# Revit family: PRD_AR_TpsAndWtrSpplOtltFttngs_FittingUnit_AQFU0230-AQFU0234 2
name_source: partatom
category: Plumbing Fixtures
units: mm (PartAtom-declared; Revit-internal decimal feet)

## family parameters
Always vertical = Yes
Cut with Voids When Loaded = No
Enable Cutting in Views = No
Maintain Annotation Orientation = No
OmniClass Number = 23.45.55.11
OmniClass Title = Sanitary Components
Part Type = Normal
Room Calculation Point = No
Round Connector Dimension = Use Diameter
Shared = No
Work Plane-Based = No

## types (5) — shared parameters
AssetType = Fixed
BodyMaterial = PRD_AR_StainlessSteel_SatinFinished
Category = Pr_40_20_87, Taps and water supply outlet fittings
Circulation = no
Export Type to IFC As = IfcDistributionChamberElementType
Finish = satin finished
Fitting = separately
FlowColdWater = 0.0 L/s
FlowHotWater = 0.0 L/s
HygieneFlushing = no
IfcExportAs = IfcDistributionChamberElement
IfcExportType = USERDEFINED
InletConversionSize = 25  [stored 0.082021 ft]
InletSize = G1B
Manufacturer = KWC Group Management AG
ManufacturerName = KWC Group Management AG
ManufacturerURL = www.kwc-professional.com
Material = stainless steel
NominalDepth = 73 mm  [stored 0.239501 ft]
NominalHeight = 470 mm  [stored 1.54199 ft]
OutletSize = 15  [stored 0.0492126 ft]
OverallDepth = 73 mm
OverallHeight = 470 mm
PipingMaterial = PRD_AR_StainlessSteel_HighPolished
PositionOfWaterConnection = from bottom
ProductInformation = http://pim.kwc.com
Status = New
Type IFC Predefined Type = USERDEFINED
TypeOfMixing = yes
TypeOfMounting = mounted on product
URL = www.kwc-professional.com
Uniclass2015Code = Pr_40_20_87
Uniclass2015Title = Taps and water supply outlet fittings
Uniclass2015Version = Products v1.38
Version = 1
WashPlaceWidth = 600 mm
zero-valued in all types: Default Elevation

## per-type parameters (varying)
| type | BIMObjectName | Description | Features | HalfWidth | ModelNumber | Name | NominalWidth | NumberOfWashPlaces | OverallWidth | Size | Width |
| AQFU0230 | PRD_AR_TapsAndWaterSupplyOutletFittings_FittingUnit_AQFU0230 | Fitting unit ready for connection with 4 wash places, for mounting on double-row sanitary facilities, for connection to hot and cold water from below via guide pipe holders. Housing made of stainless steel, satin finished with pre-assembled fitting connection blocks, connection options for power supply to electronic fittings, and stainless steel piping. | With 4 wash places, housing width 1200 mm. Wash place width 600 mm. | 600 mm | 2030064965 | Fitting unit for double-row sanitary facilities AQFU0230 | 1200 mm  [stored 3.93701 ft] | 4 | 1,200 mm | 1200 x 470 x 73 mm (W x H x D) | 1200 mm  [stored 3.93701 ft] |
| AQFU0231 | PRD_AR_TapsAndWaterSupplyOutletFittings_FittingUnit_AQFU0231 | Fitting unit ready for connection with 6 wash places, for mounting on double-row sanitary facilities, for connection to hot and cold water from below via guide pipe holders. Housing made of stainless steel, satin finished with pre-assembled fitting connection blocks, connection options for power supply to electronic fittings, and stainless steel piping. | With 6 wash places, housing width 1800 mm. Wash place width 600 mm. | 900 mm  [stored 2.95276 ft] | 2030064966 | Fitting unit for double-row sanitary facilities AQFU0231 | 1800 mm  [stored 5.90551 ft] | 6 | 1,800 mm | 1800 x 470 x 73 mm (W x H x D) | 1800 mm  [stored 5.90551 ft] |
| AQFU0232 | PRD_AR_TapsAndWaterSupplyOutletFittings_FittingUnit_AQFU0232 | Fitting unit ready for connection with 8 wash places, for mounting on double-row sanitary facilities, for connection to hot and cold water from below via guide pipe holders. Housing made of stainless steel, satin finished with pre-assembled fitting connection blocks, connection options for power supply to electronic fittings, and stainless steel piping. | With 8 wash places, housing width 2400 mm. Wash place width 600 mm. | 1200 mm  [stored 3.93701 ft] | 2030064967 | Fitting unit for double-row sanitary facilities AQFU0232 | 2400 mm | 8 | 2,400 mm | 2400 x 470 x 73 mm (W x H x D) | 2400 mm |
| AQFU0233 | PRD_AR_TapsAndWaterSupplyOutletFittings_FittingUnit_AQFU0233 | Fitting unit ready for connection with 10 wash places, for mounting on double-row sanitary facilities, for connection to hot and cold water from below via guide pipe holders. Housing made of stainless steel, satin finished with pre-assembled fitting connection blocks, connection options for power supply to electronic fittings, and stainless steel piping. | With 10 wash places, housing width 3000 mm. Wash place width 600 mm. | 1500 mm  [stored 4.92126 ft] | 2030064969 | Fitting unit for double-row sanitary facilities AQFU0233 | 3000 mm  [stored 9.84252 ft] | 10 | 3,000 mm | 3000 x 470 x 73 mm (W x H x D) | 3000 mm  [stored 9.84252 ft] |
| AQFU0234 | PRD_AR_TapsAndWaterSupplyOutletFittings_FittingUnit_AQFU0234 | Fitting unit ready for connection with 12 wash places, for mounting on double-row sanitary facilities, for connection to hot and cold water from below via guide pipe holders. Housing made of stainless steel, satin finished with pre-assembled fitting connection blocks, connection options for power supply to electronic fittings, and stainless steel piping. | With 12 wash places, housing width 3600 mm. Wash place width 600 mm. | 1800 mm  [stored 5.90551 ft] | 2030064971 | Fitting unit for double-row sanitary facilities AQFU0234 | 3600 mm  [stored 11.811 ft] | 12 | 3,600 mm | 3600 x 470 x 73 mm (W x H x D) | 3600 mm  [stored 11.811 ft] |

note: column(s) folded — value = type name in every type: Model, ModelReference

note: [stored X ft] marks values corroborated as IEEE doubles in the binary element streams (Revit-internal decimal feet)

## geometry (parser evidence)
native form markers: Sweep x4
no freeform markers — native parametric forms only
